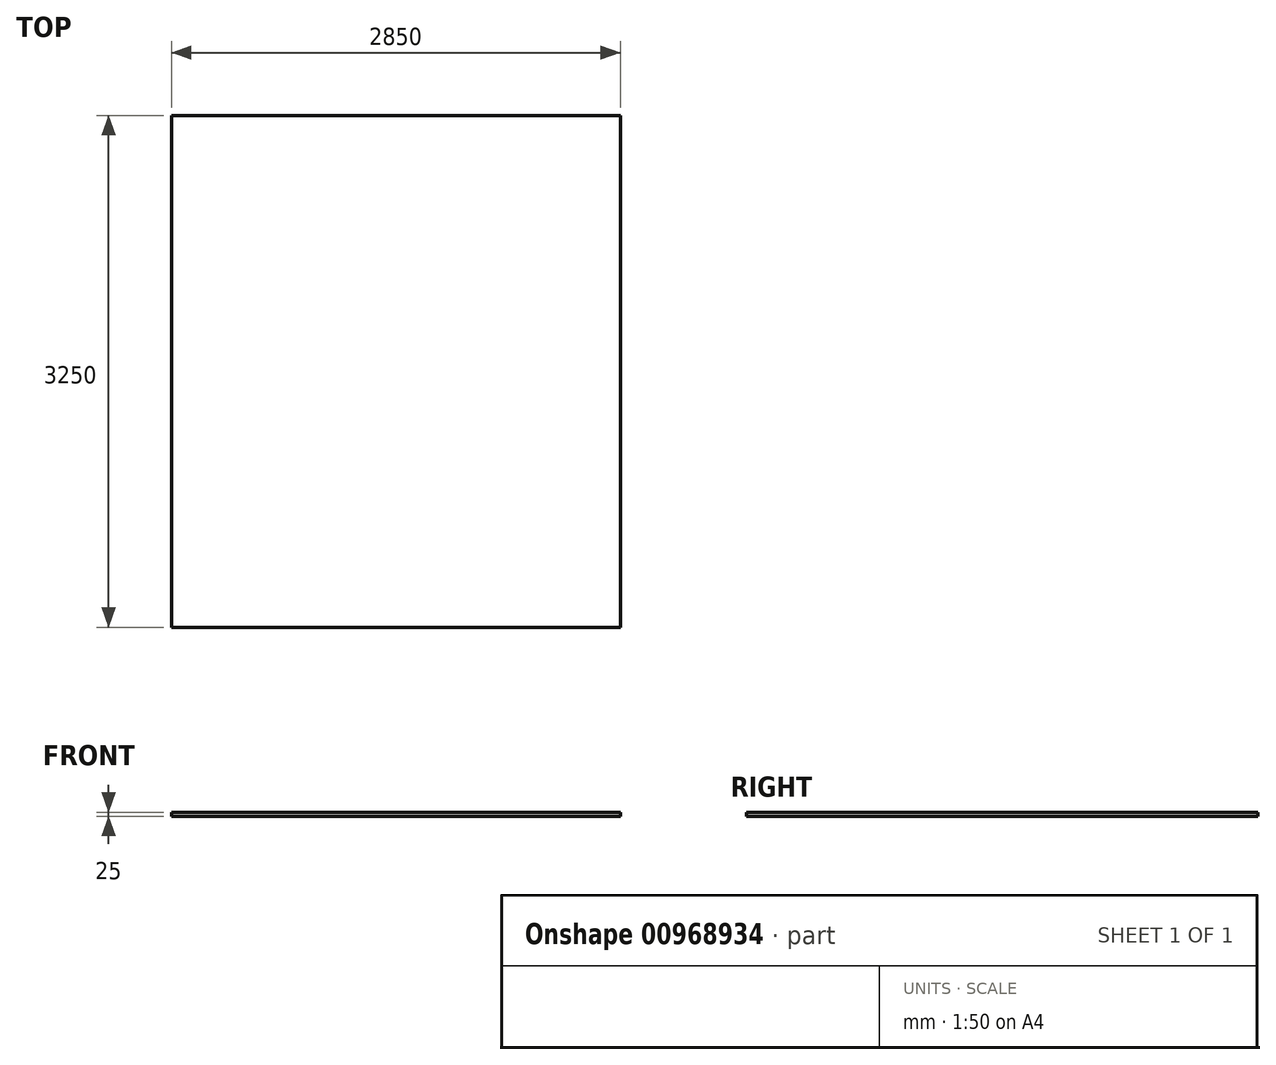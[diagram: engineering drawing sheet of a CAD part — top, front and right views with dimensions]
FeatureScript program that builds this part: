
annotation { "Feature Type Name" : "Feature", "Feature Type Description" : "" }
export const myFeature = defineFeature(function(context is Context, id is Id, definition is map)
    precondition{}
    {
        {
            var Q0;
            Q0=qCreatedBy(makeId("Top.planeOp"),FACE);
            var sketch = newSketch(context, id + "F0", { "sketchPlane" : qUnion([Q0])});
            skLineSegment(sketch, "E0.bottom", {"start": v(1425, -1625) * mm, "end": v(-1425, -1625) * mm});
            skLineSegment(sketch, "E0.top", {"start": v(1425, 1625) * mm, "end": v(-1425, 1625) * mm});
            skLineSegment(sketch, "E0.left", {"start": v(1425, -1625) * mm, "end": v(1425, 1625) * mm});
            skLineSegment(sketch, "E0.right", {"start": v(-1425, -1625) * mm, "end": v(-1425, 1625) * mm});
            skPoint(sketch, "E0.middle", {"position": v(0, 0) * mm});
            skSolve(sketch);
        }
        {
            var Q0;
            Q0=makeQuery(id+"F0.imprint","IMPRINT",FACE,{"disambiguationData":[TD([[makeQuery(id+"F0.imprint","IMPRINT",EDGE,{"derivedFrom":sQuery(id+"F0.wireOp",EDGE,"E0.bottom")}),-1.0]])]});
            extrude(context, id + "F1", {"entities" : qUnion([Q0]), "oppositeDirection" : true, "depth" : 25 * mm, "offsetDistance" : 25 * mm});
        }
    });
